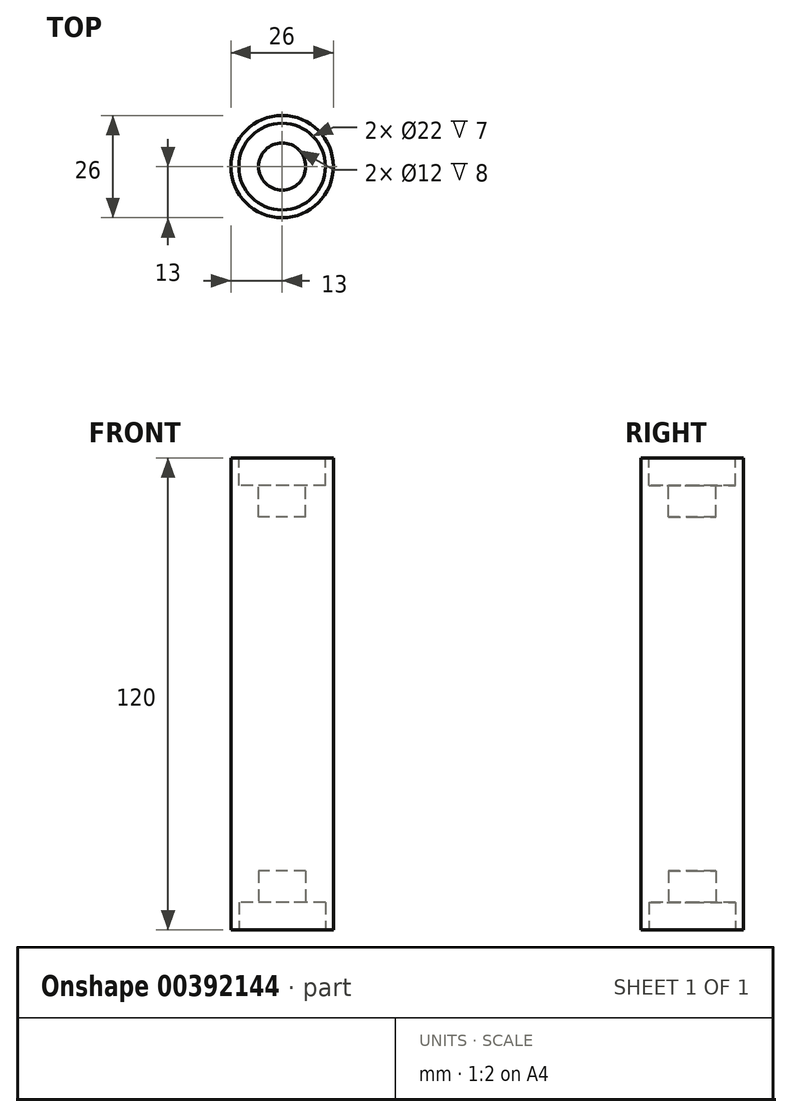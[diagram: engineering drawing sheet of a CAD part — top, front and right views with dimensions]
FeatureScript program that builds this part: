
annotation { "Feature Type Name" : "Feature", "Feature Type Description" : "" }
export const myFeature = defineFeature(function(context is Context, id is Id, definition is map)
    precondition{}
    {
        {
            var Q0;
            Q0=qCreatedBy(makeId("Top.planeOp"),FACE);
            var sketch = newSketch(context, id + "F0", { "sketchPlane" : qUnion([Q0])});
            skCircle(sketch, "E0", {"center": v(0, 0) * mm, "radius": 13 * mm});
            skCircle(sketch, "E1", {"center": v(0, 0) * mm, "radius": 6 * mm});
            skCircle(sketch, "E2", {"center": v(0, 0) * mm, "radius": 11 * mm});
            skSolve(sketch);
        }
        {
            var Q0;
            Q0 = qSketchRegion(id + "F0", true);
            var Q1;
            Q1=makeQuery(id+"F0.imprint","IMPRINT",FACE,{"disambiguationData":[TD([[makeQuery(id+"F0.imprint","IMPRINT",EDGE,{"derivedFrom":sQuery(id+"F0.wireOp",EDGE,"E1")}),-1.0]])]});
            var Q2;
            Q2=makeQuery(id+"F0.imprint","IMPRINT",FACE,{"disambiguationData":[TD([[makeQuery(id+"F0.imprint","IMPRINT",EDGE,{"derivedFrom":sQuery(id+"F0.wireOp",EDGE,"E1")}),1.0]])]});
            extrude(context, id + "F1", {"entities" : qUnion([Q0, Q1, Q2]), "depth" : 120 / 2 * mm});
        }
        {
            var Q0;
            Q0=makeQuery(id+"F0.imprint","IMPRINT",FACE,{"disambiguationData":[TD([[makeQuery(id+"F0.imprint","IMPRINT",EDGE,{"derivedFrom":sQuery(id+"F0.wireOp",EDGE,"E1")}),-1.0]])]});
            var Q1;
            Q1=makeQuery(id+"F0.imprint","IMPRINT",FACE,{"disambiguationData":[TD([[makeQuery(id+"F0.imprint","IMPRINT",EDGE,{"derivedFrom":sQuery(id+"F0.wireOp",EDGE,"E1")}),1.0]])]});
            var Q2;
            Q2=sQuery(id+"F0.wireOp",EDGE,"E1");
            var Q3;
            Q3=sQuery(id+"F0.wireOp",EDGE,"E2");
            extrude(context, id + "F2", {"entities" : qUnion([Q0, Q1]), "operationType" : NewBodyOperationType.REMOVE, "surfaceEntities" : qUnion([Q2, Q3]), "depth" : 7 * mm});
        }
        {
            var Q0;
            Q0=makeQuery(id+"F0.imprint","IMPRINT",FACE,{"disambiguationData":[TD([[makeQuery(id+"F0.imprint","IMPRINT",EDGE,{"derivedFrom":sQuery(id+"F0.wireOp",EDGE,"E1")}),1.0]])]});
            extrude(context, id + "F3", {"entities" : qUnion([Q0]), "operationType" : NewBodyOperationType.REMOVE, "depth" : (7 + 8) * mm});
        }
        {
            var Q0;
            Q0=makeQuery(id+"F1.opExtrude","CAP_FACE",FACE,{"disambiguationData":[OSD([sQuery(id+"F0.wireOp",EDGE,"E0")])],"isStart":false});
            cPlane(context, id + "F4", {"entities" : qUnion([Q0]), "cplaneType" : CPlaneType.OFFSET, "offset" : 0 * mm, "width" : 150 * mm, "height" : 150 * mm});
        }
        {
            var Q0;
            Q0=makeQuery(id+"F1.opExtrude","SWEPT_BODY",BODY,{"disambiguationData":[OSD([sQuery(id+"F0.wireOp",EDGE,"E0")])]});
            var Q1;
            Q1=qCreatedBy(id+"F4.planeOp",FACE);
            mirror(context, id + "F5", {"operationType" : NewBodyOperationType.ADD, "entities" : qUnion([Q0]), "mirrorPlane" : qUnion([Q1])});
        }
    });
